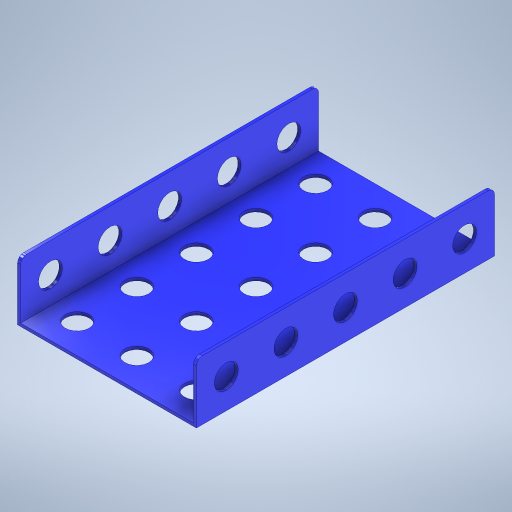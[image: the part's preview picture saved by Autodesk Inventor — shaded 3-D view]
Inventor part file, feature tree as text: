
AUTODESK INVENTOR PART (.ipt)
format: ipt  version: 2024 (Build 280153000, 153)  size: 348,672 bytes
history: native  units: mm
features: extrude x3, fillet x3, sketch x3, pattern_linear x2, other x1
ambient origin geometry x8: Origin, YZ Plane, XZ Plane, XY Plane, X Axis, Y Axis, Z Axis, Center Point
bodies: Body1 (feature_tree)
feature tree (12):
  other  "Těleso1"
  extrude  "Vysunutí1"  Depth=15.0mm
  extrude  "Vysunutí2"  Depth=15.0mm
  pattern_linear  "Obdélníkové pole1"  Spacing1=0.5mm  [1 undecoded]
  extrude  "Vysunutí3"  Depth=0.5mm
  pattern_linear  "Obdélníkové pole2"  Spacing1=0.5mm  [1 undecoded]
  fillet  "Zaoblení1"  Radius=10.0mm
  fillet  "Zaoblení2"  Radius=10.0mm
  fillet  "Zaoblení3"  Radius=50.0mm
  sketch  "Náčrt1"
  sketch  "Náčrt2"
  sketch  "Náčrt3"
note: 2 required parameter values undecoded (feature->parameter linkage not recoverable at this tier; creation-order binding heuristic only, values carry confidence <= 0.55)
